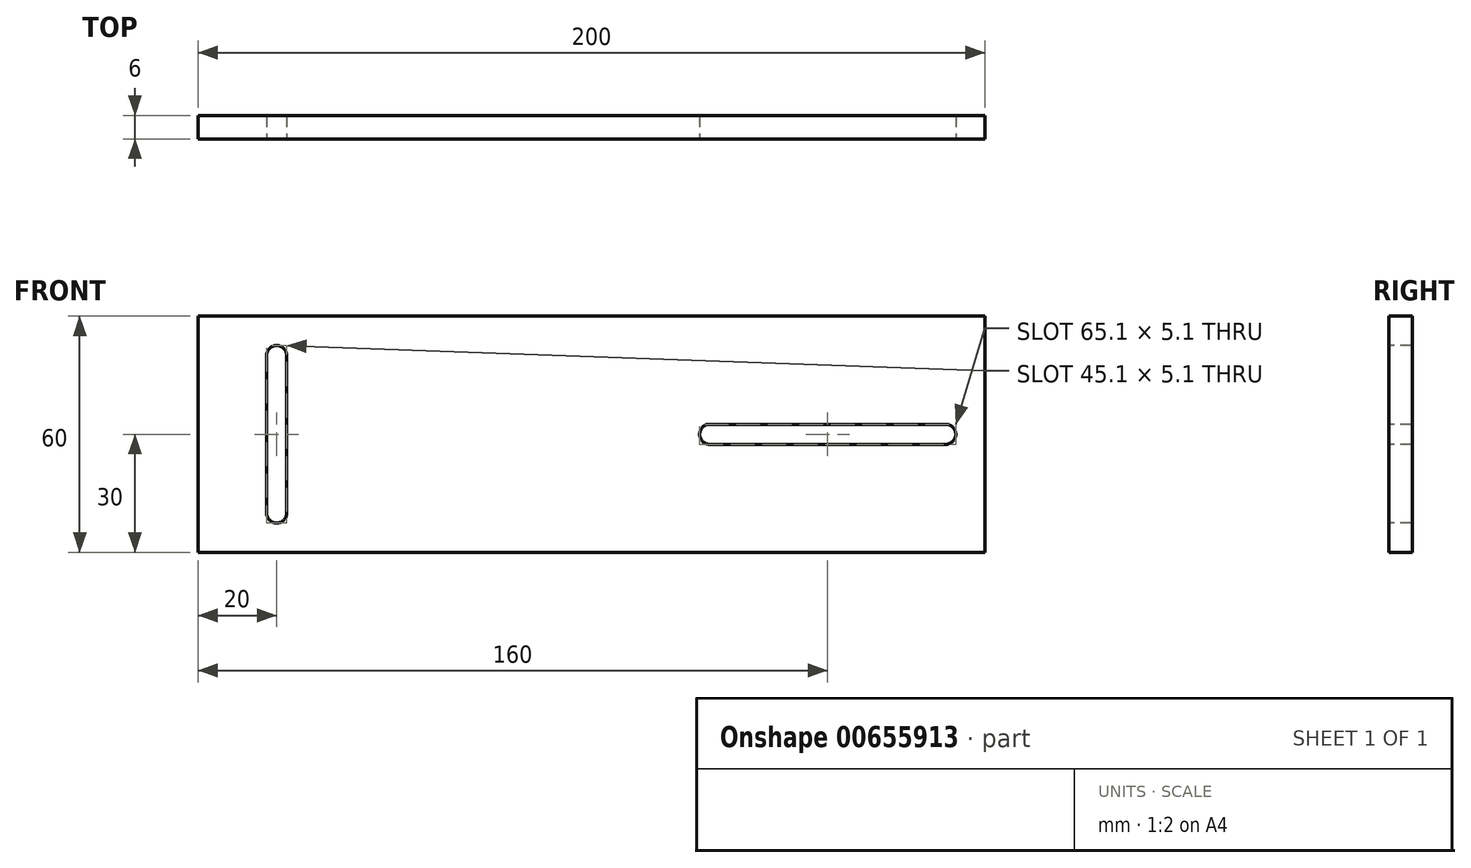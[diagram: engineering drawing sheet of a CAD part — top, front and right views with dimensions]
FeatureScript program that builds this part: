
annotation { "Feature Type Name" : "Feature", "Feature Type Description" : "" }
export const myFeature = defineFeature(function(context is Context, id is Id, definition is map)
    precondition{}
    {
        {
            var Q0;
            Q0=qCreatedBy(makeId("Front.planeOp"),FACE);
            var sketch = newSketch(context, id + "F0", { "sketchPlane" : qUnion([Q0])});
            skLineSegment(sketch, "E0.bottom", {"start": v(0, 0) * mm, "end": v(200, 0) * mm});
            skLineSegment(sketch, "E0.top", {"start": v(0, 60) * mm, "end": v(200, 60) * mm});
            skLineSegment(sketch, "E0.left", {"start": v(0, 0) * mm, "end": v(0, 60) * mm});
            skLineSegment(sketch, "E0.right", {"start": v(200, 0) * mm, "end": v(200, 60) * mm});
            skSolve(sketch);
        }
        {
            var Q0;
            Q0 = qSketchRegion(id + "F0", true);
            extrude(context, id + "F1", {"entities" : qUnion([Q0]), "depth" : 6 * mm, "offsetDistance" : 25 * mm});
        }
        {
            var Q0;
            Q0=makeQuery(id+"F1.opExtrude","CAP_FACE",FACE,{"disambiguationData":[OSD([sQuery(id+"F0.wireOp",EDGE,"E0.bottom"),sQuery(id+"F0.wireOp",EDGE,"E0.top"),sQuery(id+"F0.wireOp",EDGE,"E0.left"),sQuery(id+"F0.wireOp",EDGE,"E0.right")])],"isStart":false});
            var sketch = newSketch(context, id + "F2", { "sketchPlane" : qUnion([Q0])});
            skLineSegment(sketch, "E1", {"start": v(190, 30) * mm, "end": v(130, 30) * mm, "construction": true});
            skLineSegment(sketch, "E2", {"start": v(20, 50) * mm, "end": v(20, 10) * mm, "construction": true});
            skArc(sketch, "E3.0.startCap", {"start": v(17.45, 50) * mm, "mid": v(20, 52.55) * mm, "end": v(22.55, 50) * mm});
            skArc(sketch, "E3.0.endCap", {"start": v(22.55, 10) * mm, "mid": v(20, 7.45) * mm, "end": v(17.45, 10) * mm});
            skLineSegment(sketch, "E3.0.left", {"start": v(22.55, 50) * mm, "end": v(22.55, 10) * mm});
            skLineSegment(sketch, "E3.0.right", {"start": v(17.45, 50) * mm, "end": v(17.45, 10) * mm});
            skArc(sketch, "E3.1.startCap", {"start": v(190, 32.55) * mm, "mid": v(192.55, 30) * mm, "end": v(190, 27.45) * mm});
            skArc(sketch, "E3.1.endCap", {"start": v(130, 27.45) * mm, "mid": v(127.45, 30) * mm, "end": v(130, 32.55) * mm});
            skLineSegment(sketch, "E3.1.left", {"start": v(190, 27.45) * mm, "end": v(130, 27.45) * mm});
            skLineSegment(sketch, "E3.1.right", {"start": v(190, 32.55) * mm, "end": v(130, 32.55) * mm});
            skSolve(sketch);
        }
        {
            var Q0;
            Q0 = qSketchRegion(id + "F2", true);
            extrude(context, id + "F3", {"entities" : qUnion([Q0]), "operationType" : NewBodyOperationType.REMOVE, "endBound" : BoundingType.UP_TO_NEXT, "oppositeDirection" : true, "depth" : 25 * mm, "offsetDistance" : 25 * mm});
        }
    });
